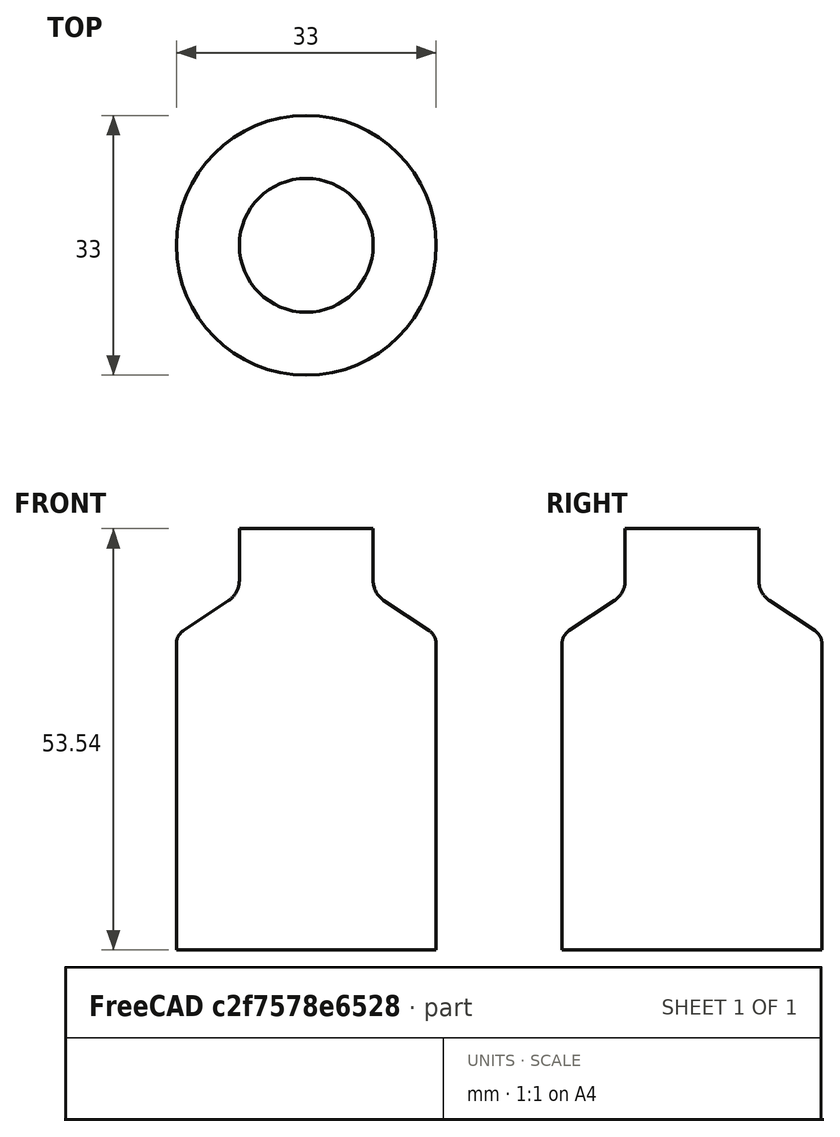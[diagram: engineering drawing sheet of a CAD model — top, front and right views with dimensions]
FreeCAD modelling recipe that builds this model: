
FCSTD DOCUMENT  (FreeCAD 0.20R29177 (Git))
Label: IntestineV3_inner
License: All rights reserved
LicenseURL: http://en.wikipedia.org/wiki/All_rights_reserved
objects: Sketcher::SketchObject×1, Part::Revolution×1
note: 2 computed .brp shape members not serialized (recipe doc carries the construction recipe); baked Part::Feature solids carry a one-line shape summary decoded from their .brp

FEATURE [Sketcher::SketchObject] Sketch
  FullyConstrained = false
  Placement = pos=(0,0,0) rot=(1,0,0;1.5708rad)
  sketch-geometry (8):
    g0: LineSegment StartX=16.5 StartY=0 StartZ=0 EndX=16.5 EndY=38.9273 EndZ=0
    g1: LineSegment StartX=8.5 StartY=53.5386 StartZ=0 EndX=8.5 EndY=46.9213 EndZ=0
    g2: LineSegment StartX=15.6064 StartY=40.5934 StartZ=0 EndX=9.84046 EndY=44.4221 EndZ=0
    g3: ArcOfCircle CenterX=11.5 CenterY=46.9213 CenterZ=0 NormalX=0 NormalY=0 NormalZ=1 AngleXU=0 Radius=3 StartAngle=3.14159 EndAngle=4.12621
    g4: GeomPoint X=8.5 Y=45.3123 Z=0
    g5: GeomPoint X=10 Y=45.3123 Z=0
    g6: ArcOfCircle CenterX=14.5 CenterY=38.9273 CenterZ=0 NormalX=0 NormalY=0 NormalZ=1 AngleXU=0 Radius=2 StartAngle=0 EndAngle=0.98462
    g7: GeomPoint X=16.5 Y=40 Z=0
  constraints (12):
    c: Vertical(g0)
    c: Vertical(g1)
    c: PointOnObject(g4,g2)
    c: PointOnObject(g4,g1)
    c: Tangent(g2,g3) = 1.5708
    c: Tangent(g1,g3) = -1.5708
    c: PointOnObject(g7,g0)
    c: PointOnObject(g7,g2)
    c: Tangent(g0,g6) = -1.5708
    c: Tangent(g2,g6) = -1.5708
    c: Radius(g3) = 3
    c: Radius(g6) = 2
FEATURE [Part::Revolution] Revolve
  Angle = 360
  Axis = (0,0,1)
  Base = (0,0,0)
  FaceMakerClass = Part::FaceMakerBullseye
  Solid = false
  Source = -> Sketch
  Symmetric = false
